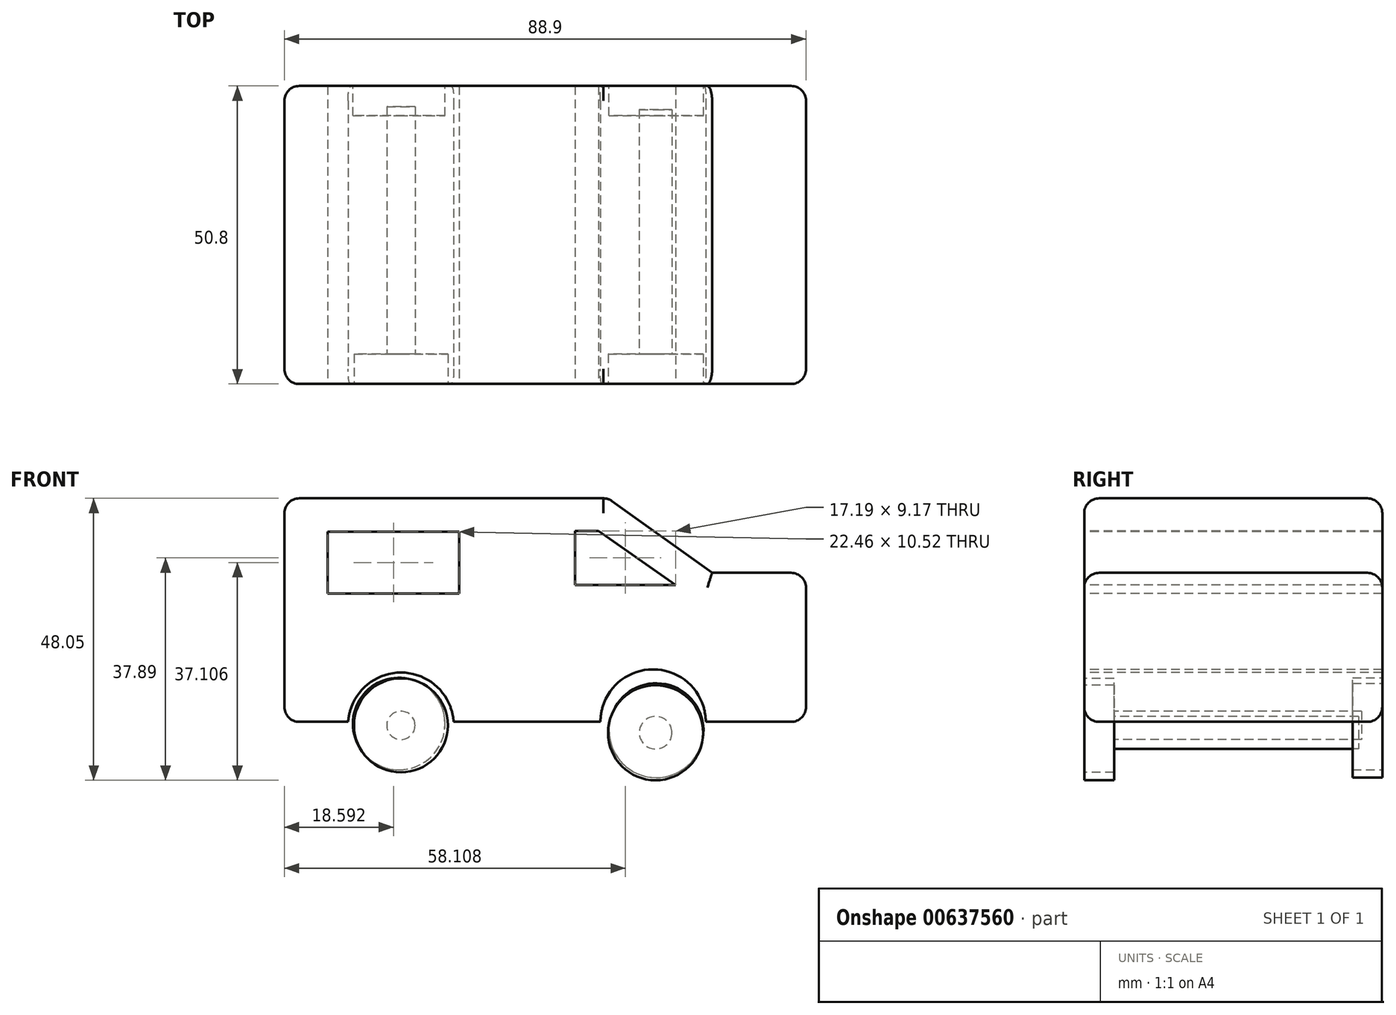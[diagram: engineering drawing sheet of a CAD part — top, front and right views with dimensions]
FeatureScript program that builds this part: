
annotation { "Feature Type Name" : "Feature", "Feature Type Description" : "" }
export const myFeature = defineFeature(function(context is Context, id is Id, definition is map)
    precondition{}
    {
        {
            var Q0;
            Q0=qCreatedBy(makeId("Front.planeOp"),FACE);
            var sketch = newSketch(context, id + "F0", { "sketchPlane" : qUnion([Q0])});
            skLineSegment(sketch, "E0", {"start": v(-65.27, 21.14) * mm, "end": v(-65.27, -16.96) * mm});
            skLineSegment(sketch, "E1", {"start": v(-65.27, -16.96) * mm, "end": v(23.63, -16.96) * mm});
            skLineSegment(sketch, "E2", {"start": v(23.63, -16.96) * mm, "end": v(23.63, 8.44) * mm});
            skLineSegment(sketch, "E3", {"start": v(23.63, 8.44) * mm, "end": v(7.63, 8.44) * mm});
            skLineSegment(sketch, "E4", {"start": v(-65.27, 21.14) * mm, "end": v(-10.09, 21.14) * mm});
            skLineSegment(sketch, "E5", {"start": v(-10.09, 21.14) * mm, "end": v(7.63, 8.44) * mm});
            skArc(sketch, "E6", {"start": v(-34.61, -16.96) * mm, "mid": v(-43.01, -8.93) * mm, "end": v(-51.42, -16.96) * mm});
            skArc(sketch, "E7", {"start": v(6.49, -16.96) * mm, "mid": v(-2.37, -9.04) * mm, "end": v(-11.22, -16.96) * mm});
            skSolve(sketch);
        }
        {
            var Q0;
            Q0 = qSketchRegion(id + "F0", true);
            extrude(context, id + "F1", {"entities" : qUnion([Q0]), "depth" : 50.8 * mm, "offsetDistance" : 25.4 * mm});
        }
        {
            var Q0;
            Q0=makeQuery(id+"F1.opExtrude","CAP_FACE",FACE,{"disambiguationData":[OSD([sQuery(id+"F0.wireOp",EDGE,"E0"),sQuery(id+"F0.wireOp",EDGE,"E1"),sQuery(id+"F0.wireOp",EDGE,"E2"),sQuery(id+"F0.wireOp",EDGE,"E3"),sQuery(id+"F0.wireOp",EDGE,"E4"),sQuery(id+"F0.wireOp",EDGE,"E5")])],"isStart":false});
            var sketch = newSketch(context, id + "F2", { "sketchPlane" : qUnion([Q0])});
            skArc(sketch, "E8", {"start": v(-36.42, -16.96) * mm, "mid": v(-45.4, -8.55) * mm, "end": v(-54.4, -16.96) * mm});
            skSolve(sketch);
        }
        {
            var Q0;
            {var subQ0=sQuery(id+"F2.wireOp",EDGE,"E8");Q0=makeQuery(id+"F2.imprint","IMPRINT",FACE,{"disambiguationData":[TD([[makeQuery(id+"F2.imprint","IMPRINT",EDGE,{"derivedFrom":subQ0}),1.0]])]});}
            extrude(context, id + "F3", {"entities" : qUnion([Q0]), "operationType" : NewBodyOperationType.REMOVE, "oppositeDirection" : true, "depth" : 50.8 * mm, "offsetDistance" : 25.4 * mm});
        }
        {
            var Q0;
            Q0=makeQuery(id+"F1.opExtrude","CAP_FACE",FACE,{"disambiguationData":[OSD([sQuery(id+"F0.wireOp",EDGE,"E0"),sQuery(id+"F0.wireOp",EDGE,"E1"),sQuery(id+"F0.wireOp",EDGE,"E2"),sQuery(id+"F0.wireOp",EDGE,"E3"),sQuery(id+"F0.wireOp",EDGE,"E4"),sQuery(id+"F0.wireOp",EDGE,"E5")])],"isStart":false});
            var sketch = newSketch(context, id + "F4", { "sketchPlane" : qUnion([Q0])});
            skArc(sketch, "E9", {"start": v(6.54, -16.96) * mm, "mid": v(-2.43, -8.01) * mm, "end": v(-11.4, -16.96) * mm});
            skSolve(sketch);
        }
        {
            var Q0;
            {var subQ0=sQuery(id+"F4.wireOp",EDGE,"E9");Q0=makeQuery(id+"F4.imprint","IMPRINT",FACE,{"disambiguationData":[TD([[makeQuery(id+"F4.imprint","IMPRINT",EDGE,{"derivedFrom":subQ0}),1.0]])]});}
            extrude(context, id + "F5", {"entities" : qUnion([Q0]), "operationType" : NewBodyOperationType.REMOVE, "oppositeDirection" : true, "depth" : 50.8 * mm, "offsetDistance" : 25.4 * mm});
        }
        {
            var Q0;
            Q0=makeQuery(id+"F1.opExtrude","CAP_FACE",FACE,{"disambiguationData":[OSD([sQuery(id+"F0.wireOp",EDGE,"E0"),sQuery(id+"F0.wireOp",EDGE,"E1"),sQuery(id+"F0.wireOp",EDGE,"E2"),sQuery(id+"F0.wireOp",EDGE,"E3"),sQuery(id+"F0.wireOp",EDGE,"E4"),sQuery(id+"F0.wireOp",EDGE,"E5")])],"isStart":false});
            var sketch = newSketch(context, id + "F6", { "sketchPlane" : qUnion([Q0])});
            skLineSegment(sketch, "E10", {"start": v(-11.74, 15.56) * mm, "end": v(1.43, 6.4) * mm});
            skLineSegment(sketch, "E11", {"start": v(1.43, 6.4) * mm, "end": v(-15.76, 6.4) * mm});
            skLineSegment(sketch, "E12", {"start": v(-15.76, 6.4) * mm, "end": v(-15.76, 15.56) * mm});
            skLineSegment(sketch, "E13", {"start": v(-15.76, 15.56) * mm, "end": v(-11.74, 15.56) * mm});
            skSolve(sketch);
        }
        {
            var Q0;
            Q0 = qSketchRegion(id + "F6", true);
            extrude(context, id + "F7", {"entities" : qUnion([Q0]), "operationType" : NewBodyOperationType.REMOVE, "oppositeDirection" : true, "depth" : 50.8 * mm, "offsetDistance" : 25.4 * mm});
        }
        {
            var Q0;
            Q0=makeQuery(id+"F1.opExtrude","CAP_FACE",FACE,{"disambiguationData":[OSD([sQuery(id+"F0.wireOp",EDGE,"E0"),sQuery(id+"F0.wireOp",EDGE,"E1"),sQuery(id+"F0.wireOp",EDGE,"E2"),sQuery(id+"F0.wireOp",EDGE,"E3"),sQuery(id+"F0.wireOp",EDGE,"E4"),sQuery(id+"F0.wireOp",EDGE,"E5")])],"isStart":false});
            var sketch = newSketch(context, id + "F8", { "sketchPlane" : qUnion([Q0])});
            skLineSegment(sketch, "E14.bottom", {"start": v(-57.9, 15.46) * mm, "end": v(-35.45, 15.46) * mm});
            skLineSegment(sketch, "E14.top", {"start": v(-57.9, 4.94) * mm, "end": v(-35.45, 4.94) * mm});
            skLineSegment(sketch, "E14.left", {"start": v(-57.9, 15.46) * mm, "end": v(-57.9, 4.94) * mm});
            skLineSegment(sketch, "E14.right", {"start": v(-35.45, 15.46) * mm, "end": v(-35.45, 4.94) * mm});
            skSolve(sketch);
        }
        {
            var Q0;
            Q0 = qSketchRegion(id + "F8", true);
            extrude(context, id + "F9", {"entities" : qUnion([Q0]), "operationType" : NewBodyOperationType.REMOVE, "oppositeDirection" : true, "depth" : 50.8 * mm, "offsetDistance" : 25.4 * mm});
        }
        {
            var Q0;
            Q0=qCreatedBy(makeId("Front.planeOp"),FACE);
            var sketch = newSketch(context, id + "F10", { "sketchPlane" : qUnion([Q0])});
            skCircle(sketch, "E15", {"center": v(-45.73, -17.28) * mm, "radius": 7.85 * mm});
            skSolve(sketch);
        }
        {
            var Q0;
            Q0 = qSketchRegion(id + "F10", true);
            extrude(context, id + "F11", {"entities" : qUnion([Q0]), "depth" : 5.08 * mm, "offsetDistance" : 25.4 * mm});
        }
        {
            var Q0;
            Q0=qCreatedBy(makeId("Front.planeOp"),FACE);
            var sketch = newSketch(context, id + "F12", { "sketchPlane" : qUnion([Q0])});
            skCircle(sketch, "E16", {"center": v(-1.89, -18.42) * mm, "radius": 8.04 * mm});
            skSolve(sketch);
        }
        {
            var Q0;
            Q0 = qSketchRegion(id + "F12", true);
            extrude(context, id + "F13", {"entities" : qUnion([Q0]), "depth" : 5.08 * mm, "offsetDistance" : 25.4 * mm});
        }
        {
            var Q0;
            Q0=makeQuery(id+"F1.opExtrude","CAP_FACE",FACE,{"disambiguationData":[OSD([sQuery(id+"F0.wireOp",EDGE,"E0"),sQuery(id+"F0.wireOp",EDGE,"E1"),sQuery(id+"F0.wireOp",EDGE,"E2"),sQuery(id+"F0.wireOp",EDGE,"E3"),sQuery(id+"F0.wireOp",EDGE,"E4"),sQuery(id+"F0.wireOp",EDGE,"E5")])],"isStart":false});
            var sketch = newSketch(context, id + "F14", { "sketchPlane" : qUnion([Q0])});
            skCircle(sketch, "E17", {"center": v(-45.4, -17.56) * mm, "radius": 8 * mm});
            skSolve(sketch);
        }
        {
            var Q0;
            Q0 = qSketchRegion(id + "F14", true);
            extrude(context, id + "F15", {"entities" : qUnion([Q0]), "oppositeDirection" : true, "depth" : 5.08 * mm, "offsetDistance" : 25.4 * mm});
        }
        {
            var Q0;
            Q0=makeQuery(id+"F1.opExtrude","CAP_FACE",FACE,{"disambiguationData":[OSD([sQuery(id+"F0.wireOp",EDGE,"E0"),sQuery(id+"F0.wireOp",EDGE,"E1"),sQuery(id+"F0.wireOp",EDGE,"E2"),sQuery(id+"F0.wireOp",EDGE,"E3"),sQuery(id+"F0.wireOp",EDGE,"E4"),sQuery(id+"F0.wireOp",EDGE,"E5")])],"isStart":false});
            var sketch = newSketch(context, id + "F16", { "sketchPlane" : qUnion([Q0])});
            skCircle(sketch, "E18", {"center": v(-2, -18.8) * mm, "radius": 8.1 * mm});
            skSolve(sketch);
        }
        {
            var Q0;
            Q0=makeQuery(id+"F16.imprint","IMPRINT",FACE,{"disambiguationData":[TD([[makeQuery(id+"F16.imprint","IMPRINT",EDGE,{"derivedFrom":sQuery(id+"F16.wireOp",EDGE,"E18")}),1.0]])]});
            extrude(context, id + "F17", {"entities" : qUnion([Q0]), "oppositeDirection" : true, "depth" : 5.08 * mm, "offsetDistance" : 25.4 * mm});
        }
        {
            var Q0;
            Q0=makeQuery(id+"F1.opExtrude","CAP_EDGE",EDGE,{"disambiguationData":[OSD([sQuery(id+"F0.wireOp",EDGE,"E4")])],"isStart":false});
            fillet(context, id + "F18", {"entities" : qUnion([Q0]), "radius" : 2.54 * mm, "tangentPropagation" : true, "allowEdgeOverflow" : false});
        }
        {
            var Q0;
            Q0=makeQuery(id+"F1.opExtrude","CAP_EDGE",EDGE,{"disambiguationData":[OSD([sQuery(id+"F0.wireOp",EDGE,"E4")])],"isStart":true});
            fillet(context, id + "F19", {"entities" : qUnion([Q0]), "radius" : 2.54 * mm, "tangentPropagation" : true, "allowEdgeOverflow" : false});
        }
        {
            var Q0;
            Q0=makeQuery(id+"F1.opExtrude","CAP_EDGE",EDGE,{"disambiguationData":[OSD([sQuery(id+"F0.wireOp",EDGE,"E3")])],"isStart":true});
            fillet(context, id + "F20", {"entities" : qUnion([Q0]), "radius" : 2.54 * mm, "tangentPropagation" : true, "allowEdgeOverflow" : false});
        }
        {
            var Q0;
            Q0=makeQuery(id+"F1.opExtrude","SWEPT_EDGE",EDGE,{"disambiguationData":[OSD([sQuery(id+"F0.wireOp",EDGE,"E2"),sQuery(id+"F0.wireOp",EDGE,"E3")])]});
            var Q1;
            Q1=makeQuery(id+"F1.opExtrude","CAP_EDGE",EDGE,{"disambiguationData":[OSD([sQuery(id+"F0.wireOp",EDGE,"E2")])],"isStart":false});
            fillet(context, id + "F21", {"entities" : qUnion([Q0, Q1]), "radius" : 2.54 * mm, "tangentPropagation" : true, "allowEdgeOverflow" : false});
        }
        {
            var Q0;
            Q0=makeQuery(id+"F1.opExtrude","SWEPT_EDGE",EDGE,{"disambiguationData":[OSD([sQuery(id+"F0.wireOp",EDGE,"E1"),sQuery(id+"F0.wireOp",EDGE,"E2")])]});
            fillet(context, id + "F22", {"entities" : qUnion([Q0]), "radius" : 2.54 * mm, "tangentPropagation" : true, "allowEdgeOverflow" : false});
        }
        {
            var Q0;
            Q0=makeQuery(id+"F1.opExtrude","CAP_EDGE",EDGE,{"disambiguationData":[OSD([sQuery(id+"F0.wireOp",EDGE,"E5")])],"isStart":false});
            fillet(context, id + "F23", {"entities" : qUnion([Q0]), "radius" : 2.54 * mm, "tangentPropagation" : true, "allowEdgeOverflow" : false});
        }
        {
            var Q0;
            Q0=makeQuery(id+"F1.opExtrude","CAP_EDGE",EDGE,{"disambiguationData":[OSD([sQuery(id+"F0.wireOp",EDGE,"E3")])],"isStart":false});
            fillet(context, id + "F24", {"entities" : qUnion([Q0]), "radius" : 2.54 * mm, "tangentPropagation" : true, "allowEdgeOverflow" : false});
        }
        {
            var Q0;
            {var subQ0=sQuery(id+"F0.wireOp",EDGE,"E2");var subQ1=sQuery(id+"F0.wireOp",EDGE,"E1");var subQ4=makeQuery(id+"F3.opExtrude","SWEPT_FACE",FACE,{"disambiguationData":[OSD([sQuery(id+"F2.wireOp",EDGE,"E8")])]});Q0=makeQuery(id+"F5.boolean.opBoolean","SPLIT",EDGE,{"disambiguationData":[TD([makeQuery(id+"F3.boolean.opBoolean","COPY",FACE,{"derivedFrom":subQ4})])],"derivedFrom":makeQuery(id+"F3.boolean.opBoolean","SPLIT",EDGE,{"disambiguationData":[TD([makeQuery(id+"F1.opExtrude","SWEPT_FACE",FACE,{"disambiguationData":[OSD([subQ0])]})])],"derivedFrom":makeQuery(id+"F1.opExtrude","CAP_EDGE",EDGE,{"disambiguationData":[OSD([subQ1])],"isStart":false})})});}
            fillet(context, id + "F25", {"entities" : qUnion([Q0]), "radius" : 2.54 * mm, "tangentPropagation" : true, "allowEdgeOverflow" : false});
        }
        {
            var Q0;
            {var subQ0=sQuery(id+"F0.wireOp",EDGE,"E0");var subQ1=sQuery(id+"F0.wireOp",EDGE,"E1");Q0=makeQuery(id+"F3.boolean.opBoolean","SPLIT",EDGE,{"disambiguationData":[TD([makeQuery(id+"F1.opExtrude","SWEPT_FACE",FACE,{"disambiguationData":[OSD([subQ0])]})])],"derivedFrom":makeQuery(id+"F1.opExtrude","CAP_EDGE",EDGE,{"disambiguationData":[OSD([subQ1])],"isStart":false})});}
            fillet(context, id + "F26", {"entities" : qUnion([Q0]), "radius" : 2.54 * mm, "tangentPropagation" : true, "allowEdgeOverflow" : false});
        }
        {
            var Q0;
            Q0=makeQuery(id+"F1.opExtrude","CAP_EDGE",EDGE,{"disambiguationData":[OSD([sQuery(id+"F0.wireOp",EDGE,"E0")])],"isStart":false});
            fillet(context, id + "F27", {"entities" : qUnion([Q0]), "radius" : 2.54 * mm, "tangentPropagation" : true, "allowEdgeOverflow" : false});
        }
        {
            var Q0;
            {var subQ0=sQuery(id+"F0.wireOp",EDGE,"E2");var subQ1=sQuery(id+"F0.wireOp",EDGE,"E1");var subQ4=makeQuery(id+"F3.opExtrude","SWEPT_FACE",FACE,{"disambiguationData":[OSD([sQuery(id+"F2.wireOp",EDGE,"E8")])]});Q0=makeQuery(id+"F5.boolean.opBoolean","SPLIT",EDGE,{"disambiguationData":[TD([makeQuery(id+"F3.boolean.opBoolean","COPY",FACE,{"derivedFrom":subQ4})])],"derivedFrom":makeQuery(id+"F3.boolean.opBoolean","SPLIT",EDGE,{"disambiguationData":[TD([makeQuery(id+"F1.opExtrude","SWEPT_FACE",FACE,{"disambiguationData":[OSD([subQ0])]})])],"derivedFrom":makeQuery(id+"F1.opExtrude","CAP_EDGE",EDGE,{"disambiguationData":[OSD([subQ1])],"isStart":true})})});}
            fillet(context, id + "F28", {"entities" : qUnion([Q0]), "radius" : 2.54 * mm, "tangentPropagation" : true, "allowEdgeOverflow" : false});
        }
        {
            var Q0;
            {var subQ0=sQuery(id+"F0.wireOp",EDGE,"E0");var subQ1=sQuery(id+"F0.wireOp",EDGE,"E1");Q0=makeQuery(id+"F3.boolean.opBoolean","SPLIT",EDGE,{"disambiguationData":[TD([makeQuery(id+"F1.opExtrude","SWEPT_FACE",FACE,{"disambiguationData":[OSD([subQ0])]})])],"derivedFrom":makeQuery(id+"F1.opExtrude","CAP_EDGE",EDGE,{"disambiguationData":[OSD([subQ1])],"isStart":true})});}
            fillet(context, id + "F29", {"entities" : qUnion([Q0]), "radius" : 2.54 * mm, "tangentPropagation" : true, "allowEdgeOverflow" : false});
        }
        {
            var Q0;
            Q0=makeQuery(id+"F15.opExtrude","CAP_FACE",FACE,{"disambiguationData":[OSD([sQuery(id+"F14.wireOp",EDGE,"E17")])],"isStart":false});
            var sketch = newSketch(context, id + "F30", { "sketchPlane" : qUnion([Q0])});
            skCircle(sketch, "E19", {"center": v(45.4, -17.56) * mm, "radius": 2.41 * mm});
            skSolve(sketch);
        }
        {
            var Q0;
            Q0 = qSketchRegion(id + "F30", true);
            extrude(context, id + "F31", {"entities" : qUnion([Q0]), "depth" : 42.16 * mm, "offsetDistance" : 25.4 * mm});
        }
        {
            var Q0;
            Q0=makeQuery(id+"F17.opExtrude","CAP_FACE",FACE,{"disambiguationData":[OSD([sQuery(id+"F16.wireOp",EDGE,"E18")])],"isStart":false});
            var sketch = newSketch(context, id + "F32", { "sketchPlane" : qUnion([Q0])});
            skCircle(sketch, "E20", {"center": v(2, -18.8) * mm, "radius": 2.78 * mm});
            skSolve(sketch);
        }
        {
            var Q0;
            Q0 = qSketchRegion(id + "F32", true);
            extrude(context, id + "F33", {"entities" : qUnion([Q0]), "depth" : 41.66 * mm, "offsetDistance" : 25.4 * mm});
        }
    });
